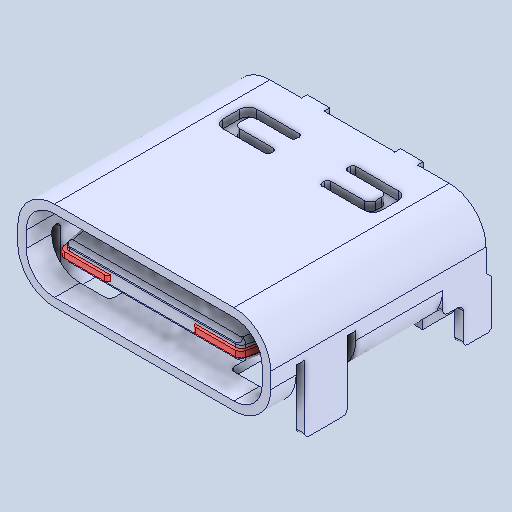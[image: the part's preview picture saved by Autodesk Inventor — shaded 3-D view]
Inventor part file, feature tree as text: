
AUTODESK INVENTOR PART (.ipt)
format: ipt  version: 2022 (Build 260153000, 153)  size: 499,200 bytes
history: mixed  units: in
note: dims shown in document units (in); Inventor stores cm internally (conversion verified against a paired STEP export)
features: other x29, mirror x1, imported_body x1
ambient origin geometry x8: Origin, YZ Plane, XZ Plane, XY Plane, X Axis, Y Axis, Z Axis, Center Point
bodies: Solid1 (imported_parasolid), Solid2 (imported_parasolid), Solid3 (imported_parasolid), Solid4 (imported_parasolid), Solid5 (imported_parasolid), Solid6 (imported_parasolid), Solid7 (imported_parasolid), Solid8 (imported_parasolid), Solid9 (imported_parasolid), Solid10 (imported_parasolid), Solid11 (imported_parasolid), Solid12 (imported_parasolid), Solid13 (imported_parasolid), Solid14 (imported_parasolid), Solid15 (imported_parasolid), Solid16 (imported_parasolid), Solid17 (imported_parasolid), Solid18 (imported_parasolid), Solid19 (imported_parasolid), Solid20 (imported_parasolid), Solid21 (imported_parasolid), Solid22 (imported_parasolid), Solid23 (imported_parasolid), Solid24 (imported_parasolid), Solid25 (imported_parasolid), Solid26 (imported_parasolid), Solid27 (imported_parasolid), Solid28 (imported_parasolid), Solid29 (imported_parasolid), Solid30 (imported_parasolid)
feature tree (31):
  mirror  "Mirror1"
  other  "Cut-Extrude5[1]"
  other  "Cut-Extrude5[2]"
  other  "Cut-Extrude5[3]"
  other  "Cut-Extrude5[4]"
  other  "Cut-Extrude5[5]"
  other  "Cut-Extrude5[6]"
  other  "Cut-Extrude5[7]"
  other  "Cut-Extrude5[8]"
  other  "Cut-Extrude5[9]"
  other  "Cut-Extrude5[10]"
  other  "Cut-Extrude5[11]"
  other  "Cut-Extrude5[12]"
  other  "Cut-Extrude5[13]"
  other  "Cut-Extrude5[14]"
  other  "Cut-Extrude6[1]"
  other  "Cut-Extrude6[2]"
  other  "Cut-Extrude6[3]"
  other  "Cut-Extrude6[4]"
  other  "Cut-Extrude6[5]"
  other  "Cut-Extrude6[6]"
  other  "Cut-Extrude6[7]"
  other  "Cut-Extrude6[8]"
  other  "Cut-Extrude6[9]"
  other  "Cut-Extrude6[10]"
  other  "Cut-Extrude6[11]"
  other  "Cut-Extrude6[12]"
  other  "Boss-Extrude8[1]"
  other  "Boss-Extrude8[2]"
  other  "Cut-Extrude10"
  imported_body  NMx_Import_Brep_tag  [imported B-rep: ~184 faces, bbox_mm=[7.92, 2.13, 6.6]]
